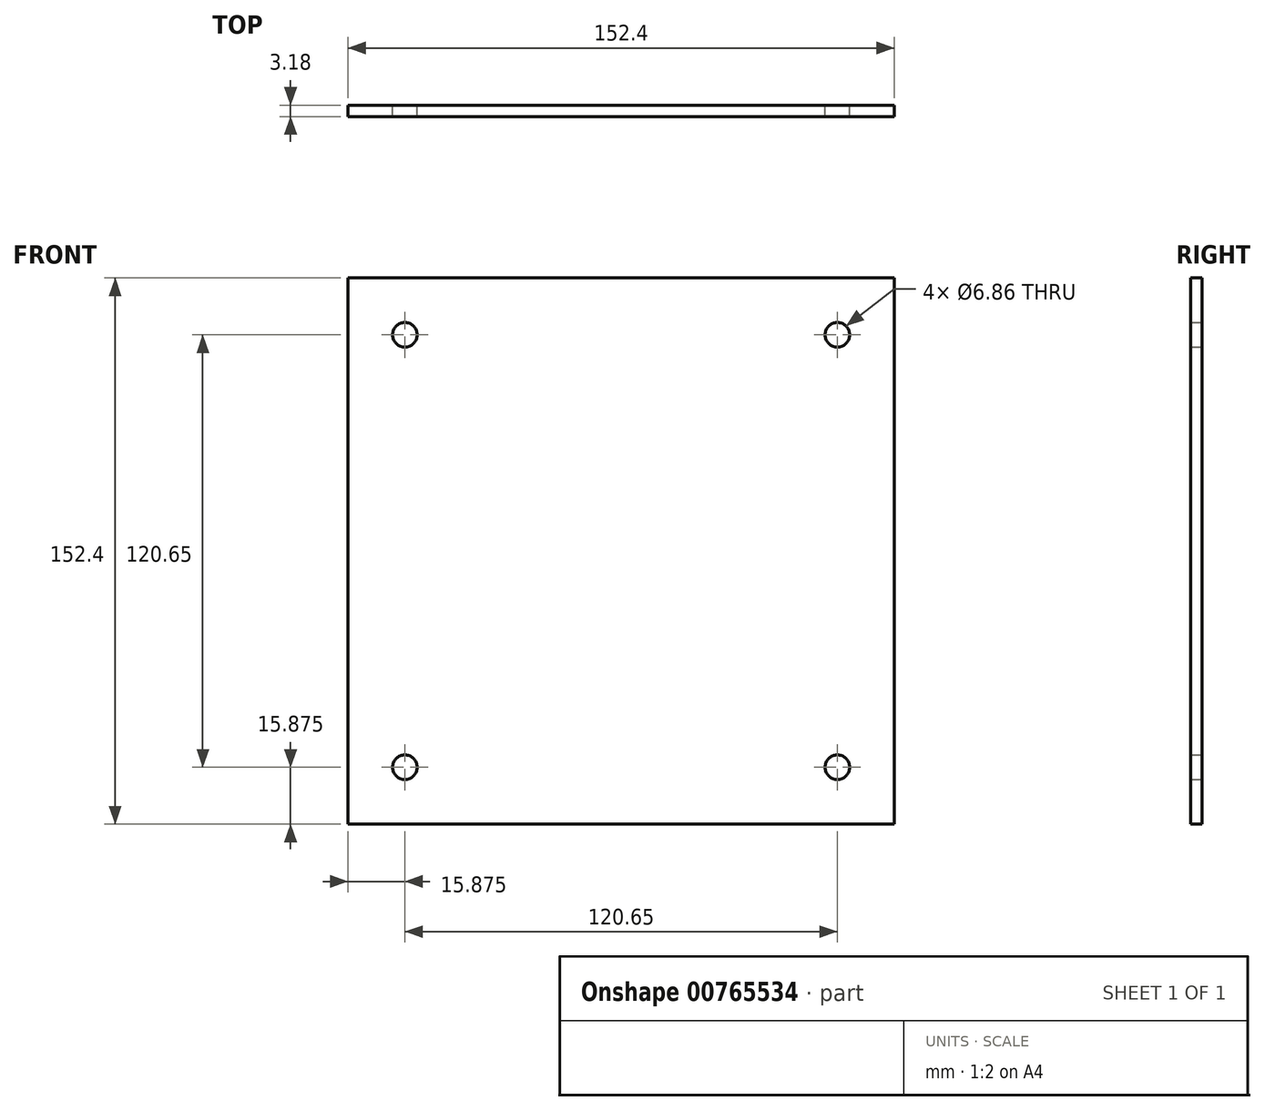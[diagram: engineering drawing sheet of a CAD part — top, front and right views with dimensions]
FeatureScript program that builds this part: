
annotation { "Feature Type Name" : "Feature", "Feature Type Description" : "" }
export const myFeature = defineFeature(function(context is Context, id is Id, definition is map)
    precondition{}
    {
        {
            var Q0;
            Q0=qCreatedBy(makeId("Front.planeOp"),FACE);
            var sketch = newSketch(context, id + "F0", { "sketchPlane" : qUnion([Q0])});
            skLineSegment(sketch, "E0.bottom", {"start": v(0, 0) * mm, "end": v(152.4, 0) * mm});
            skLineSegment(sketch, "E0.top", {"start": v(0, 152.4) * mm, "end": v(152.4, 152.4) * mm});
            skLineSegment(sketch, "E0.left", {"start": v(0, 0) * mm, "end": v(0, 152.4) * mm});
            skLineSegment(sketch, "E0.right", {"start": v(152.4, 0) * mm, "end": v(152.4, 152.4) * mm});
            skSolve(sketch);
        }
        {
            var Q0;
            Q0 = qSketchRegion(id + "F0", true);
            var sketch = newSketch(context, id + "F1", { "sketchPlane" : qUnion([Q0])});
            skCircle(sketch, "E1", {"center": v(136.52, 136.52) * mm, "radius": 3.43 * mm});
            skCircle(sketch, "E2", {"center": v(15.88, 136.52) * mm, "radius": 3.43 * mm});
            skCircle(sketch, "E3", {"center": v(15.88, 15.88) * mm, "radius": 3.43 * mm});
            skCircle(sketch, "E4", {"center": v(136.52, 15.88) * mm, "radius": 3.43 * mm});
            skLineSegment(sketch, "E5", {"start": v(0, 152.4) * mm, "end": v(152.4, 0) * mm, "construction": true});
            skLineSegment(sketch, "E6.bottom", {"start": v(136.52, 136.52) * mm, "end": v(15.88, 136.52) * mm, "construction": true});
            skLineSegment(sketch, "E6.top", {"start": v(136.52, 15.88) * mm, "end": v(15.88, 15.88) * mm, "construction": true});
            skLineSegment(sketch, "E6.left", {"start": v(136.52, 136.52) * mm, "end": v(136.52, 15.88) * mm, "construction": true});
            skLineSegment(sketch, "E6.right", {"start": v(15.88, 136.52) * mm, "end": v(15.88, 15.88) * mm, "construction": true});
            skPoint(sketch, "E6.middle", {"position": v(76.2, 76.2) * mm});
            skSolve(sketch);
        }
        {
            var Q0;
            Q0=makeQuery(id+"F1.imprint","IMPRINT",FACE,{"disambiguationData":[TD([[makeQuery(id+"F1.imprint","IMPRINT",EDGE,{"derivedFrom":sQuery(id+"F1.wireOp",EDGE,"E1")}),-1.0]])]});
            extrude(context, id + "F2", {"entities" : qUnion([Q0]), "depth" : 3.17 * mm, "offsetDistance" : 25.4 * mm});
        }
    });
